# Revit family: BIMLIB_АлюминеваяНаружняяРешетка_Забираемый_PGC_SHUFT
name_source: partatom
category: Воздухораспределители
revit_build: Autodesk Revit 2017 (Build: 20170118_1100(x64)
units: mm (PartAtom-declared; Revit-internal decimal feet)

## family parameters
Всегда вертикально = Да
На основе рабочей плоскости = Нет
Общий = Нет
При загрузке вырезать с полостями = Нет
Размер круглого соединителя = Использовать диаметр
Тип детали = Нормальный
Точка расчета площади = Нет

## types (1)
- BIMLIB_АлюминеваяНаружняяРешетка_Забираемый_PGC_SHUFT
    ADSK_URL документации изделия = http://www.shuft.ru
    ADSK_URL страницы изделия = http://www.shuft.ru
    ADSK_Версия Revit = 2017
    ADSK_Версия семейства = v.1
    ADSK_Единица измерения = шт.
    ADSK_Завод-изготовитель = ООО «Завод ВКО» марка SHUFT
    ADSK_Материал = BIMLIB_Алюминий_SHUFT
    BL_BIM library = https://bimlib.pro
    URL = http://www.shuft.ru
    Изготовитель = ООО «Завод ВКО» марка SHUFT
    Кол-во лопастей = 5
    Описание = Алюминиевые наружные решетки для круглых каналов серии PGC обеспечивают двойную защиту систем вентиляции: специальная сетка защищает систему от попадания посторонних предметов, наклонные жалюзи препятствуют проникновению внутрь системы атмосферных осадков.
    Таблица = PGC
